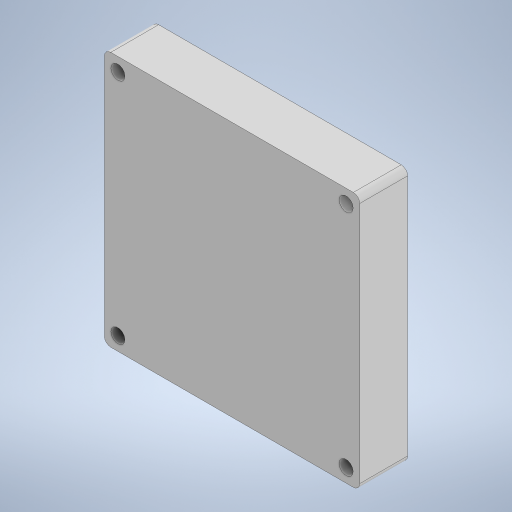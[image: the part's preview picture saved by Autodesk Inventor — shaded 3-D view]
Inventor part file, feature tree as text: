
AUTODESK INVENTOR PART (.ipt)
format: ipt  version: 2023 (Build 270158000, 158)  size: 207,872 bytes
history: native  units: in
note: dims shown in document units (in); Inventor stores cm internally (conversion verified against a paired STEP export)
features: sketch x2, extrude x1, hole x1, fillet x1
ambient origin geometry x8: Origin, YZ Plane, XZ Plane, XY Plane, X Axis, Y Axis, Z Axis, Center Point
bodies: Solid1 (feature_tree)
feature tree (5):
  extrude  "Extrusion1"  Depth=0.5906in TaperAngle=0.0deg
  hole  "Hole1"  [1 undecoded]
  fillet  "Fillet1"  [1 undecoded]
  sketch  "Sketch1"  dims[d0=3.1496in d1=0.5906in d2=0.0in]
  sketch  "Sketch2"  dims[d3=2.815in d4=0.1732in d5=0.2362in d6=0.1575in d7=0.0787in d8=90.0deg d9=0.315in d10=0.8108in d11=0.0787in]
note: 2 required parameter values undecoded (feature->parameter linkage not recoverable at this tier; creation-order binding heuristic only, values carry confidence <= 0.55)
